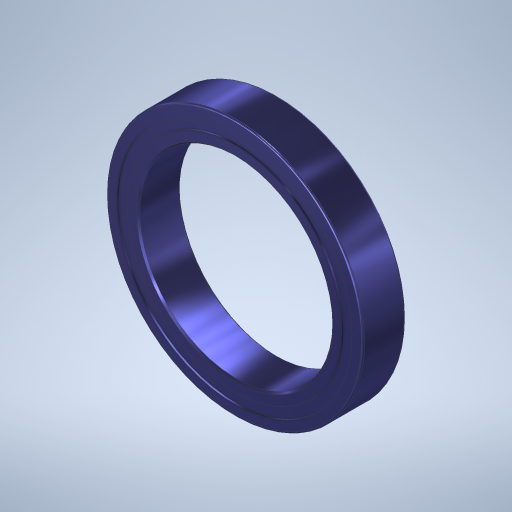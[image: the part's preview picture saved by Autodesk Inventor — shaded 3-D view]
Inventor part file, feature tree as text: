
AUTODESK INVENTOR PART (.ipt)
format: ipt  version: 2023.1 (Build 271208000, 208)  size: 334,336 bytes
history: native  units: in
note: dims shown in document units (in); Inventor stores cm internally (conversion verified against a paired STEP export)
features: extrude x2, sketch x1, fillet x1, chamfer x1
ambient origin geometry x8: Origin, YZ Plane, XZ Plane, XY Plane, X Axis, Y Axis, Z Axis, Center Point
bodies: Solid1 (feature_tree)
feature tree (5):
  sketch  "Sketch1"  dims[d0=0.5625in d1=0.032in d2=0.75in d3=0.032in d4=0.125in d5=0.0in d6=0.005in d7=0.005in d8=0.125in d9=45.0deg d10=0.115in d11=0.0in]
  extrude  "Extrusion1"  Depth=0.115in
  fillet  "Fillet1"  Radius=0.75in
  chamfer  "Chamfer1"  Distance=0.032in
  extrude  "Extrusion2"  Depth=0.125in TaperAngle=0.0deg
